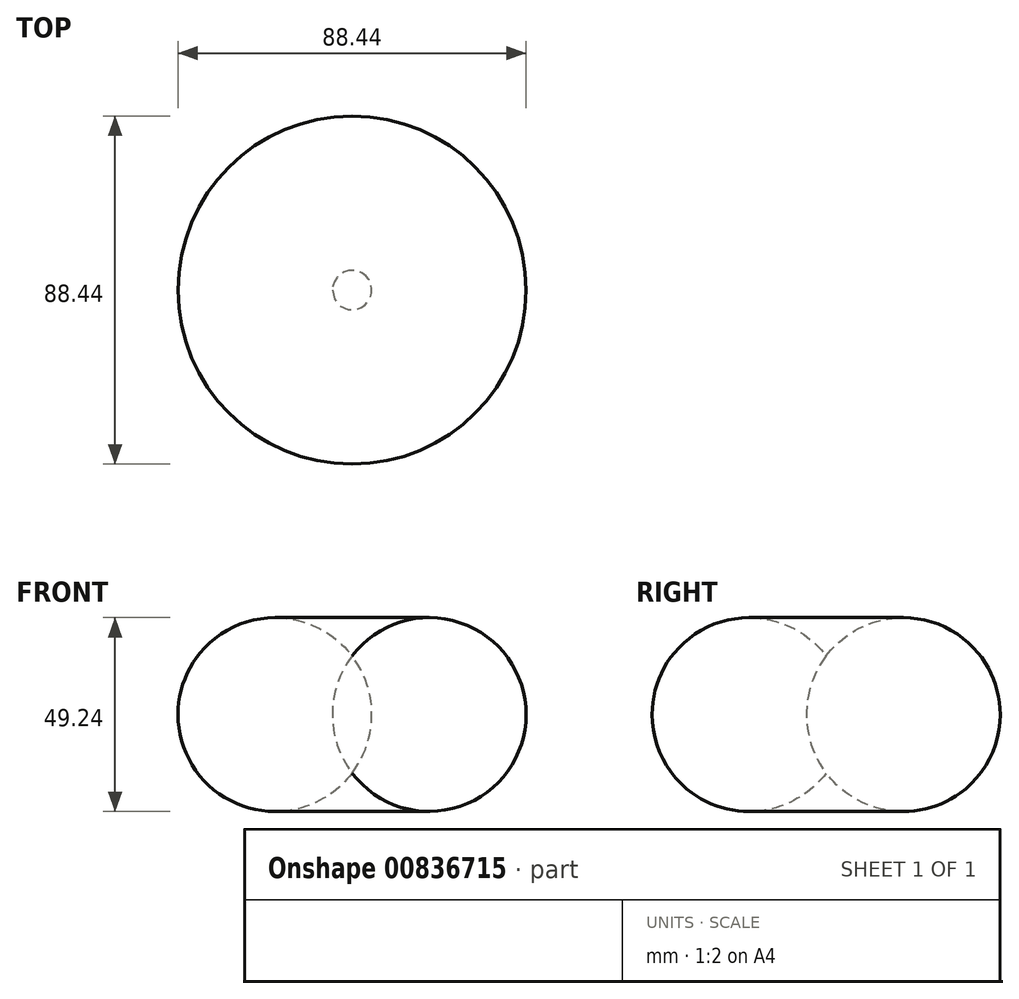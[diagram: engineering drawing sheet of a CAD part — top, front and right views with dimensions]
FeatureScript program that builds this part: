
annotation { "Feature Type Name" : "Feature", "Feature Type Description" : "" }
export const myFeature = defineFeature(function(context is Context, id is Id, definition is map)
    precondition{}
    {
        {
            var Q0;
            Q0=qCreatedBy(makeId("Front.planeOp"),FACE);
            var sketch = newSketch(context, id + "F0", { "sketchPlane" : qUnion([Q0])});
            skLineSegment(sketch, "E0", {"start": v(0, 29.78) * mm, "end": v(0, 0) * mm});
            skArc(sketch, "E1", {"start": v(0, 29.78) * mm, "mid": v(-5.01, 14.89) * mm, "end": v(0, 0) * mm});
            skArc(sketch, "E2.MirrorCS", {"start": v(0, 29.78) * mm, "mid": v(5.01, 14.89) * mm, "end": v(0, 0) * mm});
            skSolve(sketch);
        }
        {
            var Q0;
            Q0=makeQuery(id+"F0.imprint","IMPRINT",FACE,{"disambiguationData":[TD([[makeQuery(id+"F0.imprint","IMPRINT",EDGE,{"derivedFrom":sQuery(id+"F0.wireOp",EDGE,"E0")}),1.0]])]});
            var Q1;
            Q1=sQuery(id+"F0.wireOp",EDGE,"E0");
            revolve(context, id + "F1", {"surfaceOperationType" : NewSurfaceOperationType.NEW, "entities" : qUnion([Q0]), "axis" : qUnion([Q1]), "revolveType" : RevolveType.FULL});
        }
    });
